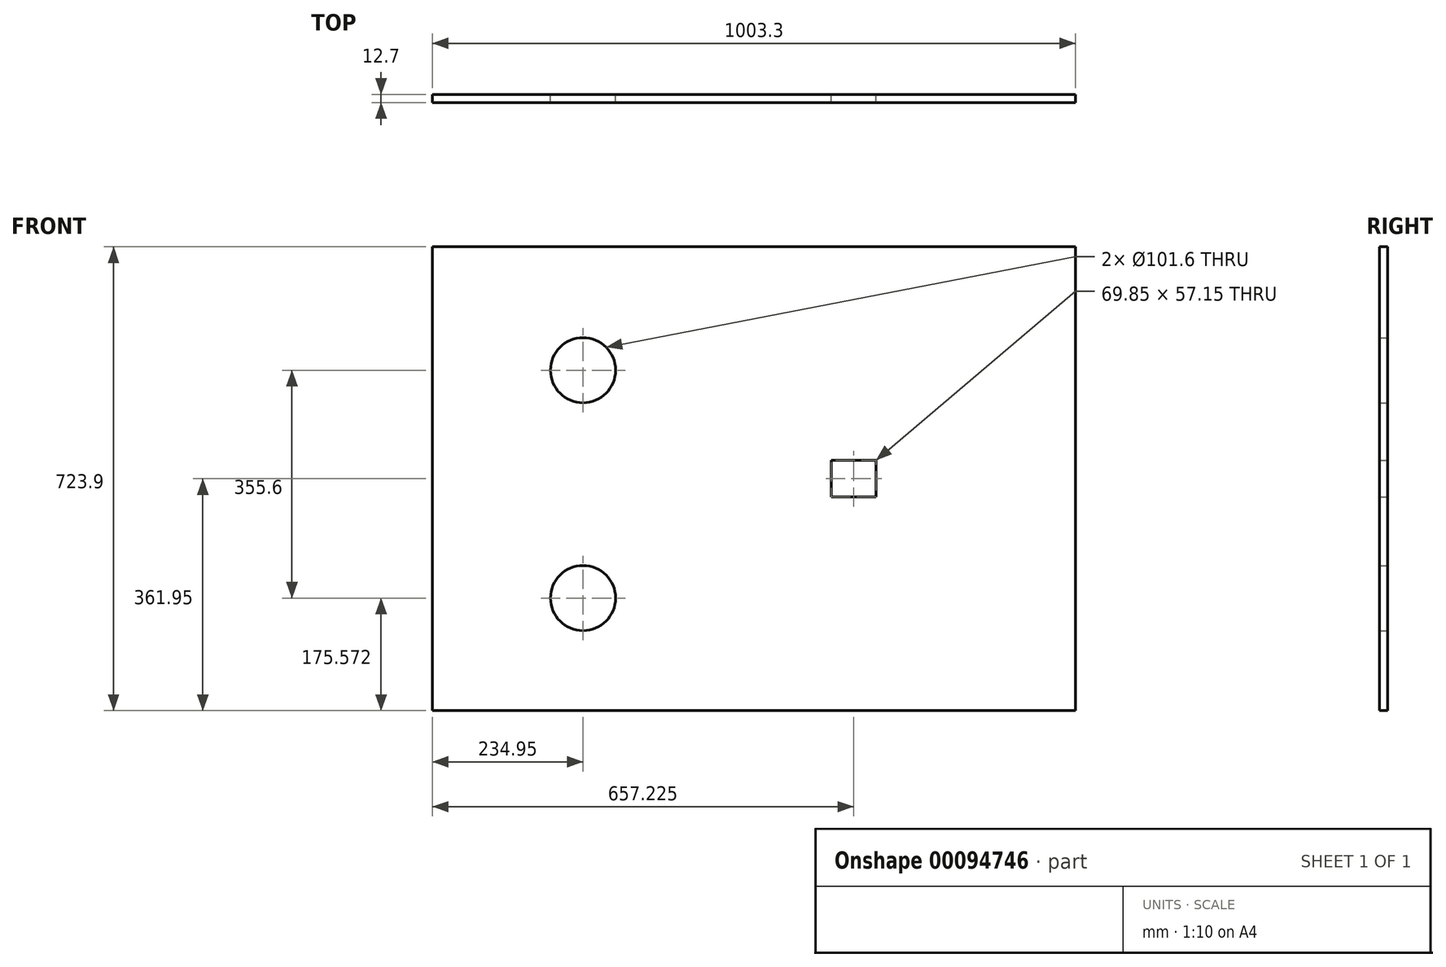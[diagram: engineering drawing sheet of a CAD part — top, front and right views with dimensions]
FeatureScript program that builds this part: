
annotation { "Feature Type Name" : "Feature", "Feature Type Description" : "" }
export const myFeature = defineFeature(function(context is Context, id is Id, definition is map)
    precondition{}
    {
        {
            var Q0;
            Q0=qCreatedBy(makeId("Front.planeOp"),FACE);
            var sketch = newSketch(context, id + "F0", { "sketchPlane" : qUnion([Q0])});
            skLineSegment(sketch, "E0.bottom", {"start": v(0, -361.95) * mm, "end": v(-1003.3, -361.95) * mm});
            skLineSegment(sketch, "E0.top", {"start": v(0, 361.95) * mm, "end": v(-1003.3, 361.95) * mm});
            skLineSegment(sketch, "E0.left", {"start": v(0, -361.95) * mm, "end": v(0, 361.95) * mm});
            skLineSegment(sketch, "E0.right", {"start": v(-1003.3, -361.95) * mm, "end": v(-1003.3, 361.95) * mm});
            skSolve(sketch);
        }
        {
            var Q0;
            Q0 = qSketchRegion(id + "F0", true);
            extrude(context, id + "F1", {"entities" : qUnion([Q0]), "depth" : 12.7 * mm});
        }
        {
            var Q0;
            Q0=qCreatedBy(makeId("Front.planeOp"),FACE);
            var sketch = newSketch(context, id + "F2", { "sketchPlane" : qUnion([Q0])});
            skLineSegment(sketch, "E1.bottom", {"start": v(-381, 28.57) * mm, "end": v(-311.15, 28.57) * mm});
            skLineSegment(sketch, "E1.top", {"start": v(-381, -28.57) * mm, "end": v(-311.15, -28.57) * mm});
            skLineSegment(sketch, "E1.left", {"start": v(-381, 28.58) * mm, "end": v(-381, -28.58) * mm});
            skLineSegment(sketch, "E1.right", {"start": v(-311.15, 28.57) * mm, "end": v(-311.15, -28.57) * mm});
            skSolve(sketch);
        }
        {
            var Q0;
            Q0 = qSketchRegion(id + "F2", true);
            extrude(context, id + "F3", {"entities" : qUnion([Q0]), "operationType" : NewBodyOperationType.REMOVE, "endBound" : BoundingType.THROUGH_ALL, "depth" : 25.4 * mm});
        }
        {
            var Q0;
            Q0=qCreatedBy(makeId("Front.planeOp"),FACE);
            var sketch = newSketch(context, id + "F4", { "sketchPlane" : qUnion([Q0])});
            skCircle(sketch, "E2", {"center": v(-768.35, 169.22) * mm, "radius": 50.8 * mm});
            skCircle(sketch, "E3", {"center": v(-768.35, -186.38) * mm, "radius": 50.8 * mm});
            skLineSegment(sketch, "E4", {"start": v(-768.35, 169.22) * mm, "end": v(-768.35, -186.38) * mm, "construction": true});
            skSolve(sketch);
        }
        {
            var Q0;
            Q0 = qSketchRegion(id + "F4", true);
            extrude(context, id + "F5", {"entities" : qUnion([Q0]), "operationType" : NewBodyOperationType.REMOVE, "endBound" : BoundingType.THROUGH_ALL, "depth" : 25.4 * mm});
        }
    });
